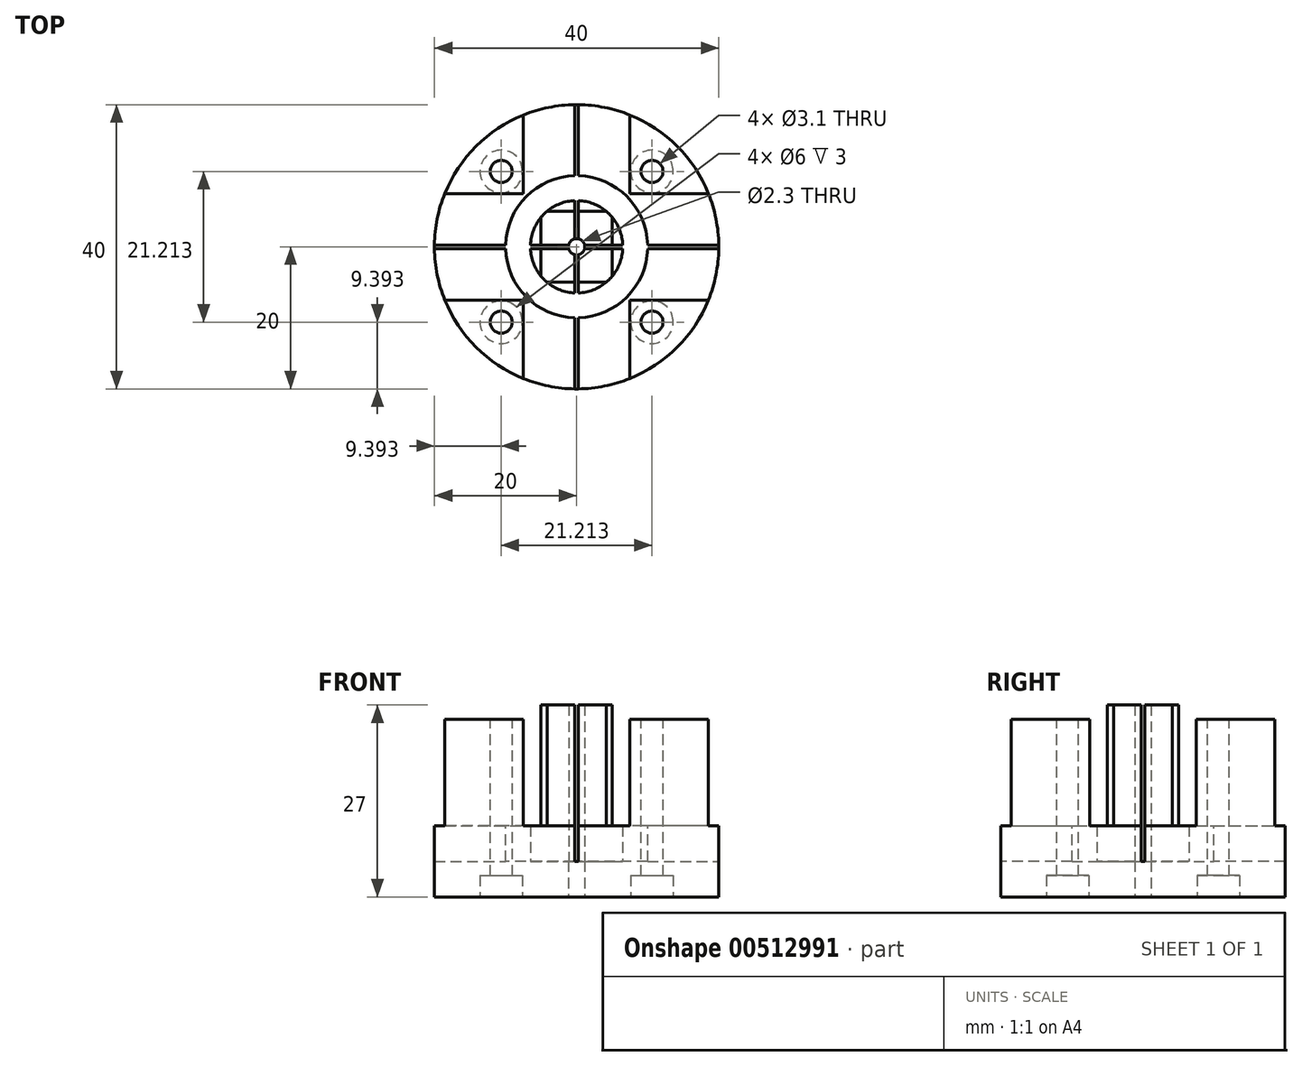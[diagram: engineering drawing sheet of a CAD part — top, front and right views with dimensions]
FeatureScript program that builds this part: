
annotation { "Feature Type Name" : "Feature", "Feature Type Description" : "" }
export const myFeature = defineFeature(function(context is Context, id is Id, definition is map)
    precondition{}
    {
        {
            var Q0;
            Q0=qCreatedBy(makeId("Top.planeOp"),FACE);
            var sketch = newSketch(context, id + "F0", { "sketchPlane" : qUnion([Q0])});
            skCircle(sketch, "E0", {"center": v(0, 0) * mm, "radius": 20 * mm});
            skSolve(sketch);
        }
        {
            var Q0;
            Q0=qSketchRegion(id+"F0",true);
            extrude(context, id + "F1", {"entities" : qUnion([Q0]), "depth" : 25 * mm});
        }
        {
            var Q0;
            Q0=makeQuery(id+"F1.opExtrude","CAP_FACE",FACE,{"disambiguationData":[OSD([sQuery(id+"F0.wireOp",EDGE,"E0")])],"isStart":false});
            var sketch = newSketch(context, id + "F2", { "sketchPlane" : qUnion([Q0])});
            skCircle(sketch, "E1", {"center": v(0, 0) * mm, "radius": 10 * mm});
            skSolve(sketch);
        }
        {
            var Q0;
            Q0=qSketchRegion(id+"F2",true);
            extrude(context, id + "F3", {"entities" : qUnion([Q0]), "operationType" : NewBodyOperationType.REMOVE, "oppositeDirection" : true, "depth" : 20 * mm});
        }
        {
            var Q0;
            {var subQ0=sQuery(id+"F0.wireOp",EDGE,"E0");var subQ1=sQuery(id+"F10.wireOp",EDGE,"E18.bottom");var subQ2=sQuery(id+"F10.wireOp",EDGE,"E15.left");var subQ3=makeQuery(id+"F10.imprint","INTERSECT",VERTEX,{"derivedFrom":[subQ2,subQ1]});var subQ7=makeQuery(id+"F1.opExtrude","CAP_EDGE",EDGE,{"disambiguationData":[OSD([subQ0])],"isStart":false});var subQ10=makeQuery(id+"F10.imprint","INTERSECT",VERTEX,{"disambiguationData":[OD(0.0)],"derivedFrom":[subQ7,subQ2]});Q0=makeQuery(id+"F11.boolean.opBoolean","SPLIT",FACE,{"disambiguationData":[TD([makeQuery(id+"F11.opExtrude","SWEPT_FACE",FACE,{"disambiguationData":[OSD([subQ2]),TDD([makeQuery(id+"F10.imprint","IMPRINT",EDGE,{"disambiguationData":[TD([[makeQuery(id+"F10.imprint","INTERSECT",VERTEX,{"derivedFrom":[sQuery(id+"F10.wireOp",EDGE,"E15.bottom"),subQ2]}),-1.0]])],"derivedFrom":subQ2}),makeQuery(id+"F10.imprint","IMPRINT",EDGE,{"disambiguationData":[TD([[subQ10,-1.0]])],"derivedFrom":subQ2}),makeQuery(id+"F10.imprint","IMPRINT",EDGE,{"disambiguationData":[TD([[subQ3,1.0]])],"derivedFrom":subQ2})])]})])],"derivedFrom":makeQuery(id+"F1.opExtrude","CAP_FACE",FACE,{"disambiguationData":[OSD([subQ0])],"isStart":false})});}
            var sketch = newSketch(context, id + "F4", { "sketchPlane" : qUnion([Q0])});
            skLineSegment(sketch, "E2", {"start": v(-21.04, 21.04) * mm, "end": v(0, 0) * mm, "construction": true});
            skLineSegment(sketch, "E3", {"start": v(0, 0) * mm, "end": v(20.97, -20.97) * mm, "construction": true});
            skLineSegment(sketch, "E4", {"start": v(0, 0) * mm, "end": v(21.21, 21.21) * mm, "construction": true});
            skLineSegment(sketch, "E5", {"start": v(0, 0) * mm, "end": v(-21.21, -21.21) * mm, "construction": true});
            skCircle(sketch, "E6", {"center": v(10.6, -10.6) * mm, "radius": 1.55 * mm});
            skCircle(sketch, "E7", {"center": v(10.6, 10.6) * mm, "radius": 1.55 * mm});
            skCircle(sketch, "E8", {"center": v(-10.6, 10.6) * mm, "radius": 1.55 * mm});
            skCircle(sketch, "E9", {"center": v(-10.6, -10.6) * mm, "radius": 1.55 * mm});
            skSolve(sketch);
        }
        {
            var Q0;
            Q0=qSketchRegion(id+"F4",true);
            extrude(context, id + "F5", {"entities" : qUnion([Q0]), "operationType" : NewBodyOperationType.REMOVE, "endBound" : BoundingType.THROUGH_ALL, "oppositeDirection" : true, "depth" : 25 * mm});
        }
        {
            var Q0;
            Q0=makeQuery(id+"F1.opExtrude","CAP_FACE",FACE,{"disambiguationData":[OSD([sQuery(id+"F0.wireOp",EDGE,"E0")])],"isStart":true});
            var sketch = newSketch(context, id + "F6", { "sketchPlane" : qUnion([Q0])});
            skCircle(sketch, "E10", {"center": v(-10.6, 10.6) * mm, "radius": 3 * mm});
            skCircle(sketch, "E11", {"center": v(10.6, 10.6) * mm, "radius": 3 * mm});
            skCircle(sketch, "E12", {"center": v(10.6, -10.6) * mm, "radius": 3 * mm});
            skCircle(sketch, "E13", {"center": v(-10.6, -10.6) * mm, "radius": 3 * mm});
            skSolve(sketch);
        }
        {
            var Q0;
            Q0=qSketchRegion(id+"F6",true);
            extrude(context, id + "F7", {"entities" : qUnion([Q0]), "operationType" : NewBodyOperationType.REMOVE, "oppositeDirection" : true, "depth" : 3 * mm});
        }
        {
            var Q0;
            Q0=makeQuery(id+"F11.boolean.opBoolean","MERGE",FACE,{"derivedFrom":[makeQuery(id+"F3.boolean.opBoolean","COPY",FACE,{"derivedFrom":makeQuery(id+"F3.opExtrude","CAP_FACE",FACE,{"disambiguationData":[OSD([sQuery(id+"F2.wireOp",EDGE,"E1")])],"isStart":false})}),makeQuery(id+"F11.opExtrude","CAP_FACE",FACE,{"disambiguationData":[OSD([sQuery(id+"F10.wireOp",EDGE,"E15.bottom"),sQuery(id+"F10.wireOp",EDGE,"E15.top"),sQuery(id+"F10.wireOp",EDGE,"E15.left"),sQuery(id+"F10.wireOp",EDGE,"E15.right"),sQuery(id+"F10.wireOp",EDGE,"E18.bottom"),sQuery(id+"F10.wireOp",EDGE,"E18.top"),sQuery(id+"F10.wireOp",EDGE,"E18.left"),sQuery(id+"F10.wireOp",EDGE,"E18.right")])],"isStart":false})]});
            var sketch = newSketch(context, id + "F8", { "sketchPlane" : qUnion([Q0])});
            skCircle(sketch, "E14", {"center": v(0, 0) * mm, "radius": 6.5 * mm});
            skSolve(sketch);
        }
        {
            var Q0;
            Q0 = qSketchRegion(id + "F8", true);
            extrude(context, id + "F9", {"entities" : qUnion([Q0]), "operationType" : NewBodyOperationType.ADD, "depth" : 22 * mm});
        }
        {
            var Q0;
            Q0=makeQuery(id+"F1.opExtrude","CAP_FACE",FACE,{"disambiguationData":[OSD([sQuery(id+"F0.wireOp",EDGE,"E0")])],"isStart":false});
            var sketch = newSketch(context, id + "F10", { "sketchPlane" : qUnion([Q0])});
            skLineSegment(sketch, "E15.bottom", {"start": v(-0.25, 21.28) * mm, "end": v(0.25, 21.28) * mm});
            skLineSegment(sketch, "E15.top", {"start": v(-0.25, -22.1) * mm, "end": v(0.25, -22.1) * mm});
            skLineSegment(sketch, "E15.left", {"start": v(-0.25, 21.28) * mm, "end": v(-0.25, -22.1) * mm});
            skLineSegment(sketch, "E15.right", {"start": v(0.25, 21.28) * mm, "end": v(0.25, -22.1) * mm});
            skLineSegment(sketch, "E16", {"start": v(0, 20) * mm, "end": v(0, -20.96) * mm, "construction": true});
            skLineSegment(sketch, "E17", {"start": v(-21.2, 0) * mm, "end": v(24.9, 0) * mm, "construction": true});
            skLineSegment(sketch, "E18.bottom", {"start": v(-22.12, 0.25) * mm, "end": v(23.6, 0.25) * mm});
            skLineSegment(sketch, "E18.top", {"start": v(-22.12, -0.25) * mm, "end": v(23.6, -0.25) * mm});
            skLineSegment(sketch, "E18.left", {"start": v(-22.12, 0.25) * mm, "end": v(-22.12, -0.25) * mm});
            skLineSegment(sketch, "E18.right", {"start": v(23.6, 0.25) * mm, "end": v(23.6, -0.25) * mm});
            skSolve(sketch);
        }
        {
            var Q0;
            Q0=qSketchRegion(id+"F10",true);
            extrude(context, id + "F11", {"entities" : qUnion([Q0]), "operationType" : NewBodyOperationType.REMOVE, "oppositeDirection" : true, "depth" : 20 * mm});
        }
        {
            var Q0;
            Q0=makeQuery(id+"F9.opExtrude","CAP_FACE",FACE,{"disambiguationData":[OSD([sQuery(id+"F8.wireOp",EDGE,"E14")])],"isStart":false});
            var sketch = newSketch(context, id + "F12", { "sketchPlane" : qUnion([Q0])});
            skLineSegment(sketch, "E19.bottom", {"start": v(0.25, 6.5) * mm, "end": v(-0.25, 6.5) * mm});
            skLineSegment(sketch, "E19.top", {"start": v(0.25, -6.5) * mm, "end": v(-0.25, -6.5) * mm});
            skLineSegment(sketch, "E19.left", {"start": v(0.25, 6.5) * mm, "end": v(0.25, -6.5) * mm});
            skLineSegment(sketch, "E19.right", {"start": v(-0.25, 6.5) * mm, "end": v(-0.25, -6.5) * mm});
            skPoint(sketch, "E19.middle", {"position": v(0, 0) * mm});
            skLineSegment(sketch, "E20.bottom", {"start": v(-6.5, 0.25) * mm, "end": v(6.5, 0.25) * mm});
            skLineSegment(sketch, "E20.top", {"start": v(-6.5, -0.25) * mm, "end": v(6.5, -0.25) * mm});
            skLineSegment(sketch, "E20.left", {"start": v(-6.5, 0.25) * mm, "end": v(-6.5, -0.25) * mm});
            skLineSegment(sketch, "E20.right", {"start": v(6.5, 0.25) * mm, "end": v(6.5, -0.25) * mm});
            skSolve(sketch);
        }
        {
            var Q0;
            Q0 = qSketchRegion(id + "F12", true);
            extrude(context, id + "F13", {"entities" : qUnion([Q0]), "operationType" : NewBodyOperationType.REMOVE, "oppositeDirection" : true, "depth" : 22 * mm});
        }
        {
            var Q0;
            {var subQ6=sQuery(id+"F0.wireOp",EDGE,"E0");Q0=makeQuery(id+"F11.boolean.opBoolean","SPLIT",FACE,{"disambiguationData":[TD([makeQuery(id+"F5.boolean.opBoolean","COPY",FACE,{"derivedFrom":makeQuery(id+"F5.opExtrude","SWEPT_FACE",FACE,{"disambiguationData":[OSD([sQuery(id+"F4.wireOp",EDGE,"E8")])]})})])],"derivedFrom":makeQuery(id+"F1.opExtrude","CAP_FACE",FACE,{"disambiguationData":[OSD([subQ6])],"isStart":false})});}
            var sketch = newSketch(context, id + "F14", { "sketchPlane" : qUnion([Q0])});
            skLineSegment(sketch, "E21.bottom", {"start": v(7.5, 5) * mm, "end": v(-7.5, 5) * mm});
            skLineSegment(sketch, "E21.top", {"start": v(7.5, 33.62) * mm, "end": v(-7.5, 33.62) * mm});
            skLineSegment(sketch, "E21.left", {"start": v(7.5, 5) * mm, "end": v(7.5, 33.62) * mm});
            skLineSegment(sketch, "E21.right", {"start": v(-7.5, 5) * mm, "end": v(-7.5, 33.62) * mm});
            skPoint(sketch, "E21.middle", {"position": v(0, 19.31) * mm});
            skLineSegment(sketch, "E22.bottom", {"start": v(7.5, -35.93) * mm, "end": v(-7.5, -35.93) * mm});
            skLineSegment(sketch, "E22.top", {"start": v(7.5, -5) * mm, "end": v(-7.5, -5) * mm});
            skLineSegment(sketch, "E22.left", {"start": v(7.5, -35.93) * mm, "end": v(7.5, -5) * mm});
            skLineSegment(sketch, "E22.right", {"start": v(-7.5, -35.93) * mm, "end": v(-7.5, -5) * mm});
            skPoint(sketch, "E22.middle", {"position": v(0, -20.47) * mm});
            skLineSegment(sketch, "E23.bottom", {"start": v(29.66, 7.5) * mm, "end": v(5, 7.5) * mm});
            skLineSegment(sketch, "E23.top", {"start": v(29.66, -7.5) * mm, "end": v(5, -7.5) * mm});
            skLineSegment(sketch, "E23.left", {"start": v(29.66, 7.5) * mm, "end": v(29.66, -7.5) * mm});
            skLineSegment(sketch, "E23.right", {"start": v(5, 7.5) * mm, "end": v(5, -7.5) * mm});
            skPoint(sketch, "E23.middle", {"position": v(17.33, 0) * mm});
            skLineSegment(sketch, "E24.bottom", {"start": v(-35, 7.5) * mm, "end": v(-5, 7.5) * mm});
            skLineSegment(sketch, "E24.top", {"start": v(-35, -7.5) * mm, "end": v(-5, -7.5) * mm});
            skLineSegment(sketch, "E24.left", {"start": v(-35, 7.5) * mm, "end": v(-35, -7.5) * mm});
            skLineSegment(sketch, "E24.right", {"start": v(-5, 7.5) * mm, "end": v(-5, -7.5) * mm});
            skPoint(sketch, "E24.middle", {"position": v(-20, 0) * mm});
            skSolve(sketch);
        }
        {
            var Q0;
            Q0 = qSketchRegion(id + "F14", true);
            extrude(context, id + "F15", {"entities" : qUnion([Q0]), "operationType" : NewBodyOperationType.REMOVE, "oppositeDirection" : true, "depth" : 15 * mm});
        }
        {
            var Q0;
            Q0 = qSketchRegion(id + "F14", true);
            extrude(context, id + "F16", {"entities" : qUnion([Q0]), "operationType" : NewBodyOperationType.REMOVE, "endBound" : BoundingType.THROUGH_ALL, "depth" : 3 * mm});
        }
        {
            var Q0;
            Q0=makeQuery(id+"F1.opExtrude","CAP_FACE",FACE,{"disambiguationData":[OSD([sQuery(id+"F0.wireOp",EDGE,"E0")])],"isStart":true});
            var sketch = newSketch(context, id + "F17", { "sketchPlane" : qUnion([Q0])});
            skCircle(sketch, "E25", {"center": v(0, 0) * mm, "radius": 1.15 * mm});
            skSolve(sketch);
        }
        {
            var Q0;
            Q0 = qSketchRegion(id + "F17", true);
            extrude(context, id + "F18", {"entities" : qUnion([Q0]), "operationType" : NewBodyOperationType.REMOVE, "endBound" : BoundingType.THROUGH_ALL, "oppositeDirection" : true, "depth" : 25 * mm, "offsetDistance" : 25 * mm});
        }
    });
